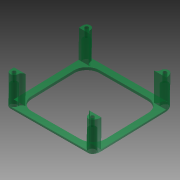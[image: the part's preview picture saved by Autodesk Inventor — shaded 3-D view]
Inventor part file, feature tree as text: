
AUTODESK INVENTOR PART (.ipt)
format: ipt  version: 2014 (Build 180170000, 170)  size: 395,264 bytes
history: native  units: in
note: dims shown in document units (in); Inventor stores cm internally (conversion verified against a paired STEP export)
features: extrude x13, sketch x13, fillet x9, projected_geometry x3, pattern_circular x1
ambient origin geometry x8: Origin, YZ Plane, XZ Plane, XY Plane, X Axis, Y Axis, Z Axis, Center Point
bodies: Solid1 (feature_tree)
feature tree (39):
  extrude  "Extrusion1"  Depth=3.7in
  extrude  "Extrusion2"  Depth=1.0in
  extrude  "Extrusion3"  Depth=0.2in TaperAngle=0.0deg
  pattern_circular  "Circular Pattern1"  Count=3 Angle=360.0deg
  extrude  "Extrusion4"  Depth=0.3in
  extrude  "Extrusion5"  Depth=3.0in
  fillet  "Fillet1"  Radius=0.135in
  fillet  "Fillet2"  Radius=0.15in
  fillet  "Fillet3"  Radius=0.15in
  extrude  "Extrusion6"  Depth=1.3in TaperAngle=0.0deg
  fillet  "Fillet4"  Radius=0.15in
  fillet  "Fillet5"  Radius=0.2in
  extrude  "Extrusion7"  Depth=0.3in
  fillet  "Fillet6"  Radius=0.7in
  fillet  "Fillet7"  Radius=0.125in
  extrude  "Extrusion8"  Depth=0.05in
  extrude  "Extrusion9"  Depth=0.15in
  fillet  "Fillet8"  Radius=0.25in
  extrude  "Extrusion11"  Depth=0.25in
  fillet  "Fillet9"  Radius=0.25in
  extrude  "Extrusion12"  Depth=0.5in
  extrude  "Extrusion13"  Depth=0.1in
  extrude  "Extrusion14"  Depth=0.25in
  sketch  "Sketch1"  dims[d0=2.6in d1=3.7in]
  sketch  "Sketch2"  dims[d2=0.2in d3=0.0in d4=1.0in]
  sketch  "Sketch3"  dims[d5=2.0in d6=0.2in d7=0.0in]
  sketch  "Sketch4"  dims[d8=0.135in]
  sketch  "Sketch5"  dims[d10=0.2in d11=0.0in d12=1.1811in d13=360.0deg]
  sketch  "Sketch6"  dims[d15=1.0in d16=0.3in]
  sketch  "Sketch7"  dims[d18=2.9in d20=3.0in d21=0.135in d22=0.15in d23=0.15in]
  sketch  "Sketch8"  dims[d24=0.15in d25=1.3in d26=0.0in d27=0.15in d28=0.2in]
  projected_geometry  "Projected Loop1"
  projected_geometry  "Projected Loop2"
  projected_geometry  "Projected Loop3"
  sketch  "Sketch9"  dims[d29=0.3in d30=0.3in d31=0.7in d32=0.0in d33=0.125in]
  sketch  "Sketch11"  dims[d34=0.125in d35=0.05in]
  sketch  "Sketch12"  dims[d36=0.15in d37=0.15in d38=0.25in]
  sketch  "Sketch13"  dims[d39=0.25in d40=0.25in d41=0.25in]
  sketch  "Sketch14"  dims[d42=0.7in d43=0.0in d44=0.5in d45=0.1in d46=0.25in d47=0.25in d48=0.25in d49=0.25in d50=0.25in d51=0.25in d52=0.7in d53=0.0in d54=1.0in d55=1.0in d56=0.1in d57=0.0in d58=0.15in d59=0.0in d62=0.05in d63=0.25in d64=0.25in d65=0.25in d66=0.25in d67=0.15in d68=0.0in d69=0.5in d70=0.0in d71=0.0in d72=0.0in d73=0.0in d74=0.283in d75=0.8in d76=0.0in]
